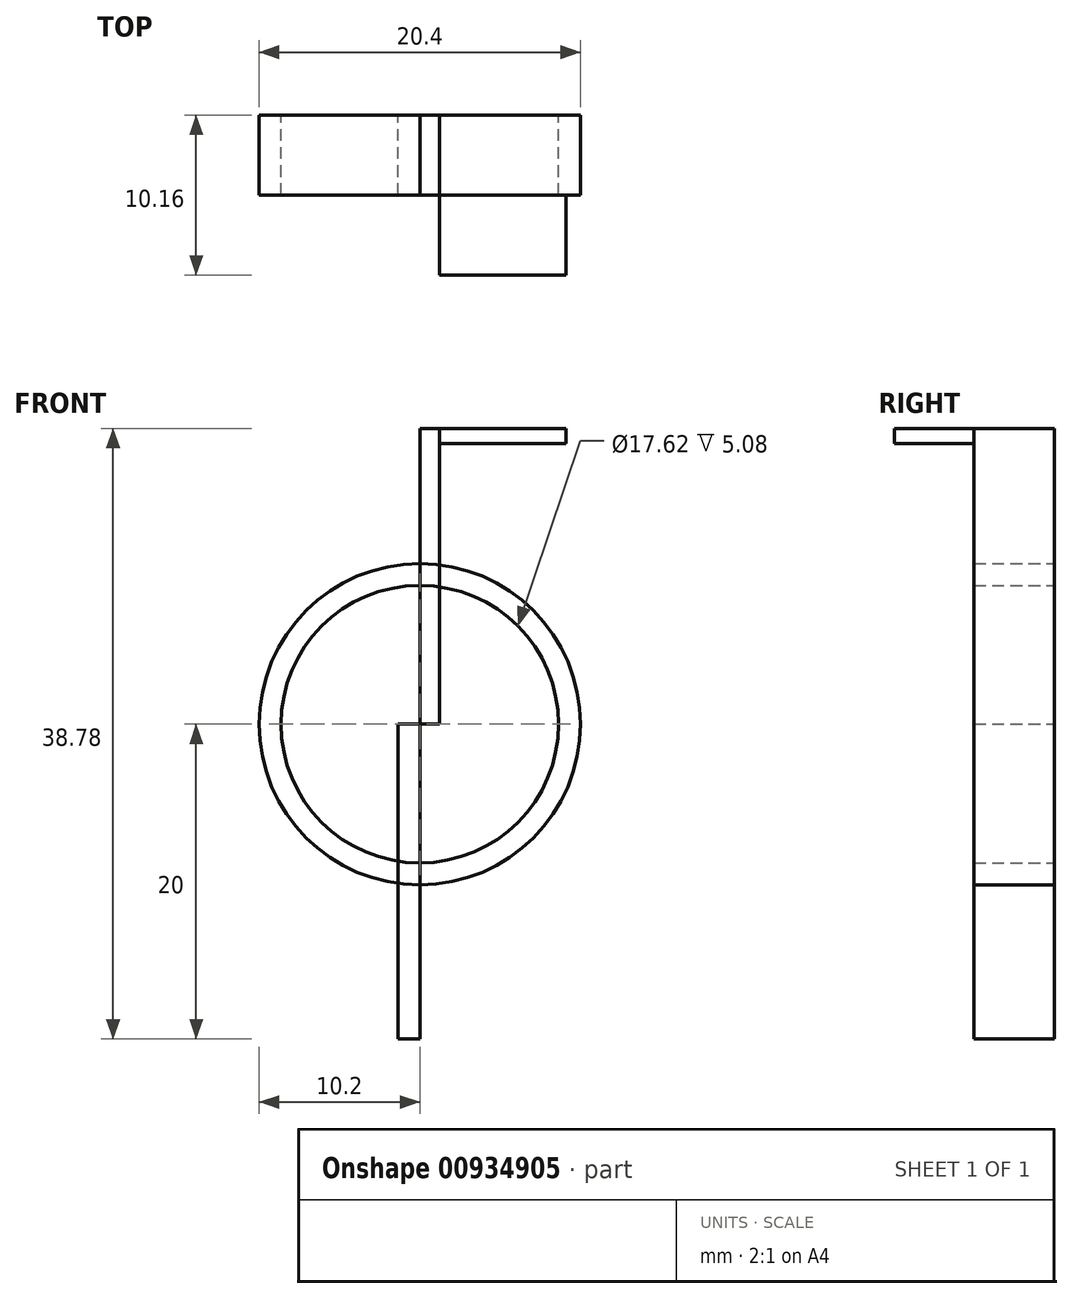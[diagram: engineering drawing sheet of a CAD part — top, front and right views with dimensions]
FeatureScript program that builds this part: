
annotation { "Feature Type Name" : "Feature", "Feature Type Description" : "" }
export const myFeature = defineFeature(function(context is Context, id is Id, definition is map)
    precondition{}
    {
        {
            var Q0;
            Q0=qCreatedBy(makeId("Front.planeOp"),FACE);
            var sketch = newSketch(context, id + "F0", { "sketchPlane" : qUnion([Q0])});
            skCircle(sketch, "E0", {"center": v(0, 0) * mm, "radius": 10.2 * mm});
            skCircle(sketch, "E1", {"center": v(0, 0) * mm, "radius": 8.81 * mm});
            skSolve(sketch);
        }
        {
            var Q0;
            Q0=makeQuery(id+"F0.imprint","IMPRINT",FACE,{"disambiguationData":[TD([[makeQuery(id+"F0.imprint","IMPRINT",EDGE,{"derivedFrom":sQuery(id+"F0.wireOp",EDGE,"E0")}),1.0]])]});
            extrude(context, id + "F1", {"entities" : qUnion([Q0]), "depth" : 5.08 * mm, "offsetDistance" : 25.4 * mm});
        }
        {
            var Q0;
            Q0=qCreatedBy(makeId("Front.planeOp"),FACE);
            var sketch = newSketch(context, id + "F2", { "sketchPlane" : qUnion([Q0])});
            skLineSegment(sketch, "E2.bottom", {"start": v(0, 0) * mm, "end": v(1.25, 0) * mm});
            skLineSegment(sketch, "E2.top", {"start": v(0, 18.78) * mm, "end": v(1.25, 18.78) * mm});
            skLineSegment(sketch, "E2.left", {"start": v(0, 0) * mm, "end": v(0, 18.78) * mm});
            skLineSegment(sketch, "E2.right", {"start": v(1.25, 0) * mm, "end": v(1.25, 18.78) * mm});
            skLineSegment(sketch, "E3.bottom", {"start": v(0, 0) * mm, "end": v(-1.38, 0) * mm});
            skLineSegment(sketch, "E3.top", {"start": v(0, -20) * mm, "end": v(-1.38, -20) * mm});
            skLineSegment(sketch, "E3.left", {"start": v(0, 0) * mm, "end": v(0, -20) * mm});
            skLineSegment(sketch, "E3.right", {"start": v(-1.38, 0) * mm, "end": v(-1.38, -20) * mm});
            skSolve(sketch);
        }
        {
            var Q0;
            Q0 = qSketchRegion(id + "F2", true);
            extrude(context, id + "F3", {"entities" : qUnion([Q0]), "depth" : 5.08 * mm, "offsetDistance" : 25.4 * mm});
        }
        {
            var Q0;
            Q0=makeQuery(id+"F3.opExtrude","CAP_FACE",FACE,{"disambiguationData":[OSD([sQuery(id+"F2.wireOp",EDGE,"E2.bottom"),sQuery(id+"F2.wireOp",EDGE,"E2.top"),sQuery(id+"F2.wireOp",EDGE,"E2.left"),sQuery(id+"F2.wireOp",EDGE,"E2.right")])],"isStart":false});
            var sketch = newSketch(context, id + "F4", { "sketchPlane" : qUnion([Q0])});
            skLineSegment(sketch, "E4.bottom", {"start": v(1.25, 18.78) * mm, "end": v(9.3, 18.78) * mm});
            skLineSegment(sketch, "E4.top", {"start": v(1.25, 17.83) * mm, "end": v(9.3, 17.83) * mm});
            skLineSegment(sketch, "E4.left", {"start": v(1.25, 18.78) * mm, "end": v(1.25, 17.83) * mm});
            skLineSegment(sketch, "E4.right", {"start": v(9.3, 18.78) * mm, "end": v(9.3, 17.83) * mm});
            skSolve(sketch);
        }
        {
            var Q0;
            Q0=makeQuery(id+"F4.imprint","IMPRINT",FACE,{"disambiguationData":[TD([[makeQuery(id+"F4.imprint","IMPRINT",EDGE,{"derivedFrom":sQuery(id+"F4.wireOp",EDGE,"E4.bottom")}),-1.0]])]});
            extrude(context, id + "F5", {"entities" : qUnion([Q0]), "depth" : 5.08 * mm, "offsetDistance" : 25.4 * mm});
        }
    });
